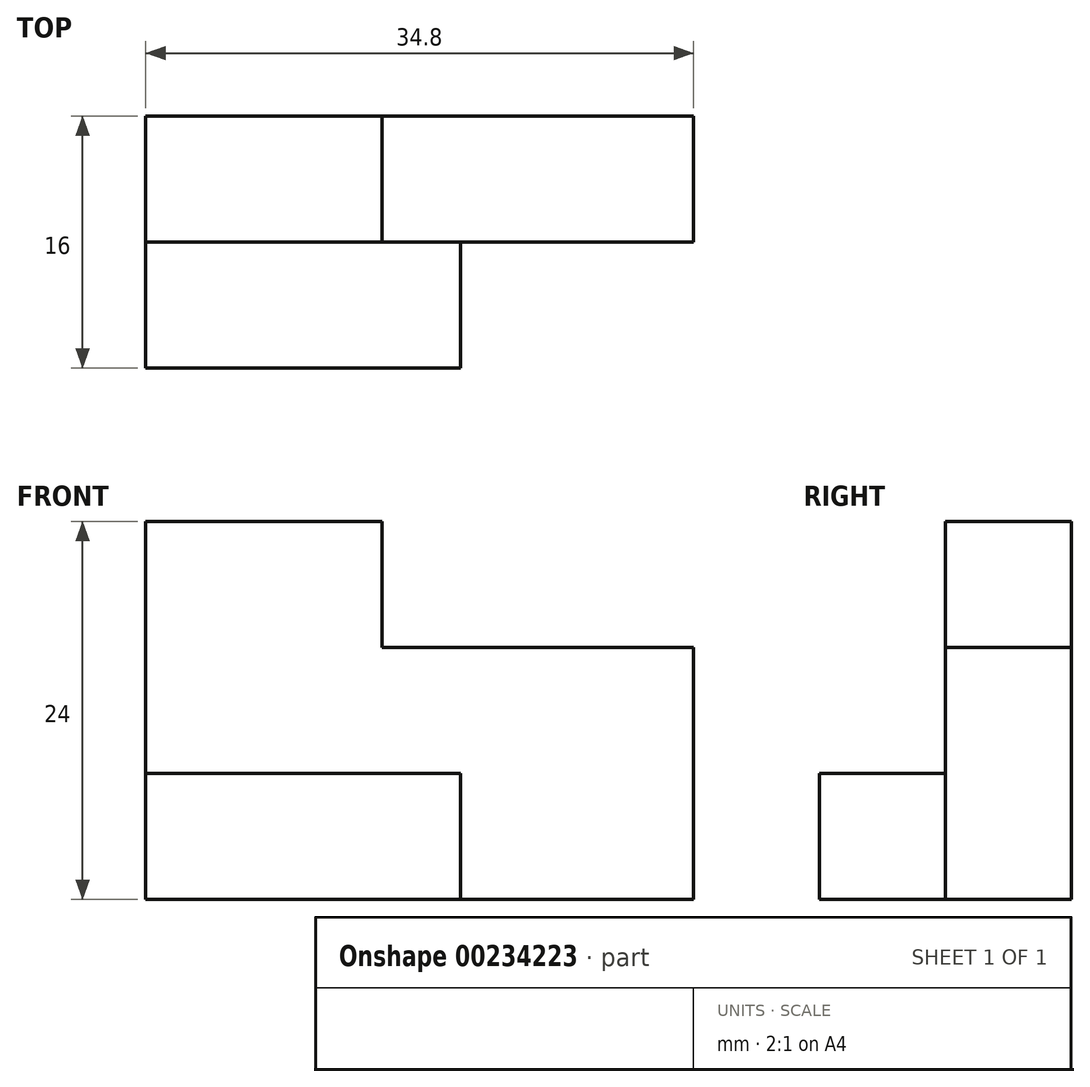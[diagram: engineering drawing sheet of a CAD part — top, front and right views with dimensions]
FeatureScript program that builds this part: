
annotation { "Feature Type Name" : "Feature", "Feature Type Description" : "" }
export const myFeature = defineFeature(function(context is Context, id is Id, definition is map)
    precondition{}
    {
        {
            var Q0;
            Q0=qCreatedBy(makeId("Top.planeOp"),FACE);
            var sketch = newSketch(context, id + "F0", { "sketchPlane" : qUnion([Q0])});
            skLineSegment(sketch, "E0", {"start": v(0, 0) * mm, "end": v(0, 8) * mm});
            skLineSegment(sketch, "E1", {"start": v(0, 8) * mm, "end": v(15, 8) * mm});
            skLineSegment(sketch, "E2", {"start": v(15, 8) * mm, "end": v(15, 0) * mm});
            skLineSegment(sketch, "E3", {"start": v(15, 0) * mm, "end": v(0, 0) * mm});
            skSolve(sketch);
        }
        {
            var Q0;
            Q0 = qSketchRegion(id + "F0", true);
            extrude(context, id + "F1", {"entities" : qUnion([Q0]), "depth" : 24 * mm});
        }
        {
            var Q0;
            Q0=makeQuery(id+"F1.opExtrude","SWEPT_FACE",FACE,{"disambiguationData":[OSD([sQuery(id+"F0.wireOp",EDGE,"E2")])]});
            var sketch = newSketch(context, id + "F2", { "sketchPlane" : qUnion([Q0])});
            skLineSegment(sketch, "E4", {"start": v(0, 24) * mm, "end": v(0, 16) * mm});
            skLineSegment(sketch, "E5", {"start": v(0, 16) * mm, "end": v(8, 16) * mm});
            skLineSegment(sketch, "E6", {"start": v(8, 16) * mm, "end": v(8, 0) * mm});
            skLineSegment(sketch, "E7", {"start": v(8, 0) * mm, "end": v(0, 0) * mm});
            skLineSegment(sketch, "E8", {"start": v(0, 0) * mm, "end": v(0, 16) * mm});
            skSolve(sketch);
        }
        {
            var Q0;
            Q0=makeQuery(id+"F2.imprint","IMPRINT",FACE,{"disambiguationData":[TD([[makeQuery(id+"F2.imprint","IMPRINT",EDGE,{"derivedFrom":sQuery(id+"F2.wireOp",EDGE,"E5")}),-1.0]])]});
            extrude(context, id + "F3", {"entities" : qUnion([Q0]), "operationType" : NewBodyOperationType.ADD, "depth" : 19.8 * mm});
        }
        {
            var Q0;
            Q0=qCreatedBy(makeId("Top.planeOp"),FACE);
            var sketch = newSketch(context, id + "F4", { "sketchPlane" : qUnion([Q0])});
            skLineSegment(sketch, "E9", {"start": v(0, 0) * mm, "end": v(0, -8) * mm});
            skLineSegment(sketch, "E10", {"start": v(0, -8) * mm, "end": v(20, -8) * mm});
            skLineSegment(sketch, "E11", {"start": v(20, -8) * mm, "end": v(20, 0) * mm});
            skLineSegment(sketch, "E12", {"start": v(0, 0) * mm, "end": v(20, 0) * mm});
            skSolve(sketch);
        }
        {
            var Q0;
            Q0 = qSketchRegion(id + "F4", true);
            extrude(context, id + "F5", {"entities" : qUnion([Q0]), "operationType" : NewBodyOperationType.ADD, "depth" : 8 * mm});
        }
    });
